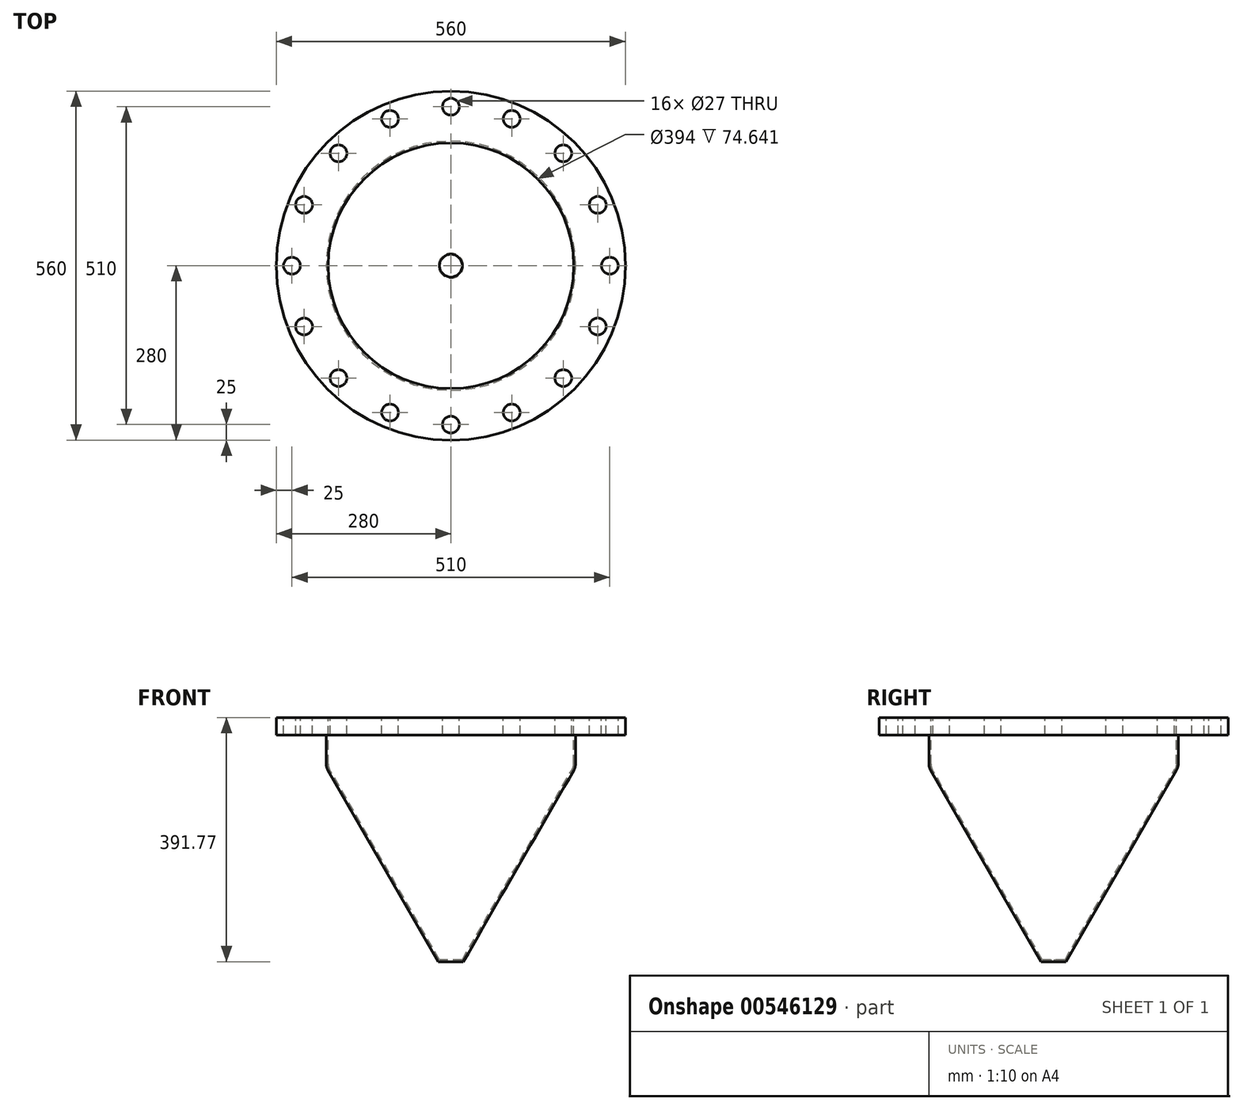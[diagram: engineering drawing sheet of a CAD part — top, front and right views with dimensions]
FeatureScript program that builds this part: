
annotation { "Feature Type Name" : "Feature", "Feature Type Description" : "" }
export const myFeature = defineFeature(function(context is Context, id is Id, definition is map)
    precondition{}
    {
        {
            var Q0;
            Q0=qCreatedBy(makeId("Top.planeOp"),FACE);
            var sketch = newSketch(context, id + "F0", { "sketchPlane" : qUnion([Q0])});
            skCircle(sketch, "E0", {"center": v(0, 0) * mm, "radius": 280 * mm});
            skCircle(sketch, "E1", {"center": v(0, 0) * mm, "radius": 200 * mm});
            skSolve(sketch);
        }
        {
            var Q0;
            Q0=qSketchRegion(id+"F0",true);
            extrude(context, id + "F1", {"entities" : qUnion([Q0]), "depth" : 28 * mm, "offsetDistance" : 25 * mm});
        }
        {
            var Q0;
            Q0=qCreatedBy(makeId("Front.planeOp"),FACE);
            var sketch = newSketch(context, id + "F2", { "sketchPlane" : qUnion([Q0])});
            skLineSegment(sketch, "E2", {"start": v(200, 28) * mm, "end": v(200, -46.64) * mm});
            skLineSegment(sketch, "E3", {"start": v(197.32, -56.64) * mm, "end": v(20, -363.77) * mm});
            skLineSegment(sketch, "E4", {"start": v(20, -363.77) * mm, "end": v(0, -363.77) * mm});
            skPoint(sketch, "E5.visualSharp", {"position": v(200, -52) * mm});
            skArc(sketch, "E5.filletArc", {"start": v(197.32, -56.64) * mm, "mid": v(199.32, -51.82) * mm, "end": v(200, -46.64) * mm});
            skLineSegment(sketch, "E6.0", {"start": v(18.27, -360.77) * mm, "end": v(0, -360.77) * mm});
            skLineSegment(sketch, "E6.1", {"start": v(194.72, -55.14) * mm, "end": v(18.27, -360.77) * mm});
            skArc(sketch, "E6.2", {"start": v(194.72, -55.14) * mm, "mid": v(196.42, -51.04) * mm, "end": v(197, -46.64) * mm});
            skLineSegment(sketch, "E6.3", {"start": v(197, 28) * mm, "end": v(197, -46.64) * mm});
            skLineSegment(sketch, "E7", {"start": v(197, 28) * mm, "end": v(200, 28) * mm});
            skLineSegment(sketch, "E8", {"start": v(0, -360.77) * mm, "end": v(0, -363.77) * mm});
            skSolve(sketch);
        }
        {
            var Q0;
            Q0 = qSketchRegion(id + "F2", true);
            var Q1;
            Q1=sQuery(id+"F2.wireOp",EDGE,"E8");
            revolve(context, id + "F3", {"operationType" : NewBodyOperationType.ADD, "entities" : qUnion([Q0]), "axis" : qUnion([Q1]), "revolveType" : RevolveType.FULL});
        }
        {
            var Q0;
            Q0=makeQuery(id+"F3.boolean.opBoolean","MERGE",FACE,{"derivedFrom":[makeQuery(id+"F1.opExtrude","CAP_FACE",FACE,{"disambiguationData":[OSD([sQuery(id+"F0.wireOp",EDGE,"E0"),sQuery(id+"F0.wireOp",EDGE,"E1")])],"isStart":false}),makeQuery(id+"F3.opRevolve","SWEPT_FACE",FACE,{"disambiguationData":[OSD([sQuery(id+"F2.wireOp",EDGE,"E7")])]})]});
            var sketch = newSketch(context, id + "F4", { "sketchPlane" : qUnion([Q0])});
            skCircle(sketch, "E9", {"center": v(255, 0) * mm, "radius": 13.5 * mm});
            skCircle(sketch, "E10.1.0", {"center": v(235.59, 97.58) * mm, "radius": 13.5 * mm});
            skCircle(sketch, "E10.2.0", {"center": v(180.31, 180.31) * mm, "radius": 13.5 * mm});
            skCircle(sketch, "E10.3.0", {"center": v(97.58, 235.59) * mm, "radius": 13.5 * mm});
            skCircle(sketch, "E10.4.0", {"center": v(0, 255) * mm, "radius": 13.5 * mm});
            skCircle(sketch, "E10.5.0", {"center": v(-97.58, 235.59) * mm, "radius": 13.5 * mm});
            skCircle(sketch, "E10.6.0", {"center": v(-180.31, 180.31) * mm, "radius": 13.5 * mm});
            skCircle(sketch, "E10.7.0", {"center": v(-235.59, 97.58) * mm, "radius": 13.5 * mm});
            skCircle(sketch, "E10.8.0", {"center": v(-255, 0) * mm, "radius": 13.5 * mm});
            skCircle(sketch, "E10.9.0", {"center": v(-235.59, -97.58) * mm, "radius": 13.5 * mm});
            skCircle(sketch, "E10.10.0", {"center": v(-180.31, -180.31) * mm, "radius": 13.5 * mm});
            skCircle(sketch, "E10.11.0", {"center": v(-97.58, -235.59) * mm, "radius": 13.5 * mm});
            skCircle(sketch, "E10.12.0", {"center": v(0, -255) * mm, "radius": 13.5 * mm});
            skCircle(sketch, "E10.13.0", {"center": v(97.58, -235.59) * mm, "radius": 13.5 * mm});
            skCircle(sketch, "E10.14.0", {"center": v(180.31, -180.31) * mm, "radius": 13.5 * mm});
            skCircle(sketch, "E10.15.0", {"center": v(235.59, -97.58) * mm, "radius": 13.5 * mm});
            skPoint(sketch, "E10.center", {"position": v(0, 0) * mm});
            skSolve(sketch);
        }
        {
            var Q0;
            Q0 = qSketchRegion(id + "F4", true);
            extrude(context, id + "F5", {"entities" : qUnion([Q0]), "operationType" : NewBodyOperationType.REMOVE, "endBound" : BoundingType.UP_TO_NEXT, "oppositeDirection" : true, "depth" : 25 * mm, "offsetDistance" : 25 * mm});
        }
    });
